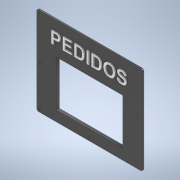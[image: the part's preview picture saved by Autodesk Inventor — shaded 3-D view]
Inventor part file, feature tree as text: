
AUTODESK INVENTOR PART (.ipt)
format: ipt  version: 2020 (Build 240168000, 168)  size: 405,504 bytes
history: native  units: mm
features: extrude x4, sketch x4, fillet x1, chamfer x1, other x1
ambient origin geometry x8: Origin, YZ Plane, XZ Plane, XY Plane, X Axis, Y Axis, Z Axis, Center Point
bodies: Solid1 (feature_tree)
feature tree (11):
  extrude  "Extrusion1"  Depth=250.0mm
  fillet  "Fillet1"  Radius=4.0mm
  extrude  "Extrusion5"  Depth=33.5mm
  chamfer  "Chamfer2"  Distance=122.0mm
  sketch  "Sketch7"  dims[d55=90.075mm]
  extrude  "Extrusion6"  Depth=2.0mm
  extrude  "Extrusion7"  Depth=2.0mm TaperAngle=0.0deg
  other  "Front-CNC-CUT"
  sketch  "Sketch1"  dims[d0=300.0mm d1=250.0mm d2=4.0mm d3=0.0mm]
  sketch  "Sketch5"  dims[d4=5.0mm d54=33.5mm]
  sketch  "Sketch8"  dims[d56=90.075mm d57=122.0mm d58=180.15mm d59=81.3mm d60=0.0mm d64=4.0mm d65=2.0mm d66=45.0deg d70=5.0mm d71=10.0mm d72=5.0mm d73=81.3mm d74=0.0mm d75=2.0mm d76=0.0mm d81=10.0mm d82=5.0mm d83=10.0mm d84=5.0mm d85=10.0mm d86=5.0mm d87=10.0mm d88=5.0mm d93=250.0mm d94=300.0mm d48=0.5mm d49=0.872665mm d50=0.5mm d51=0.872665mm]
